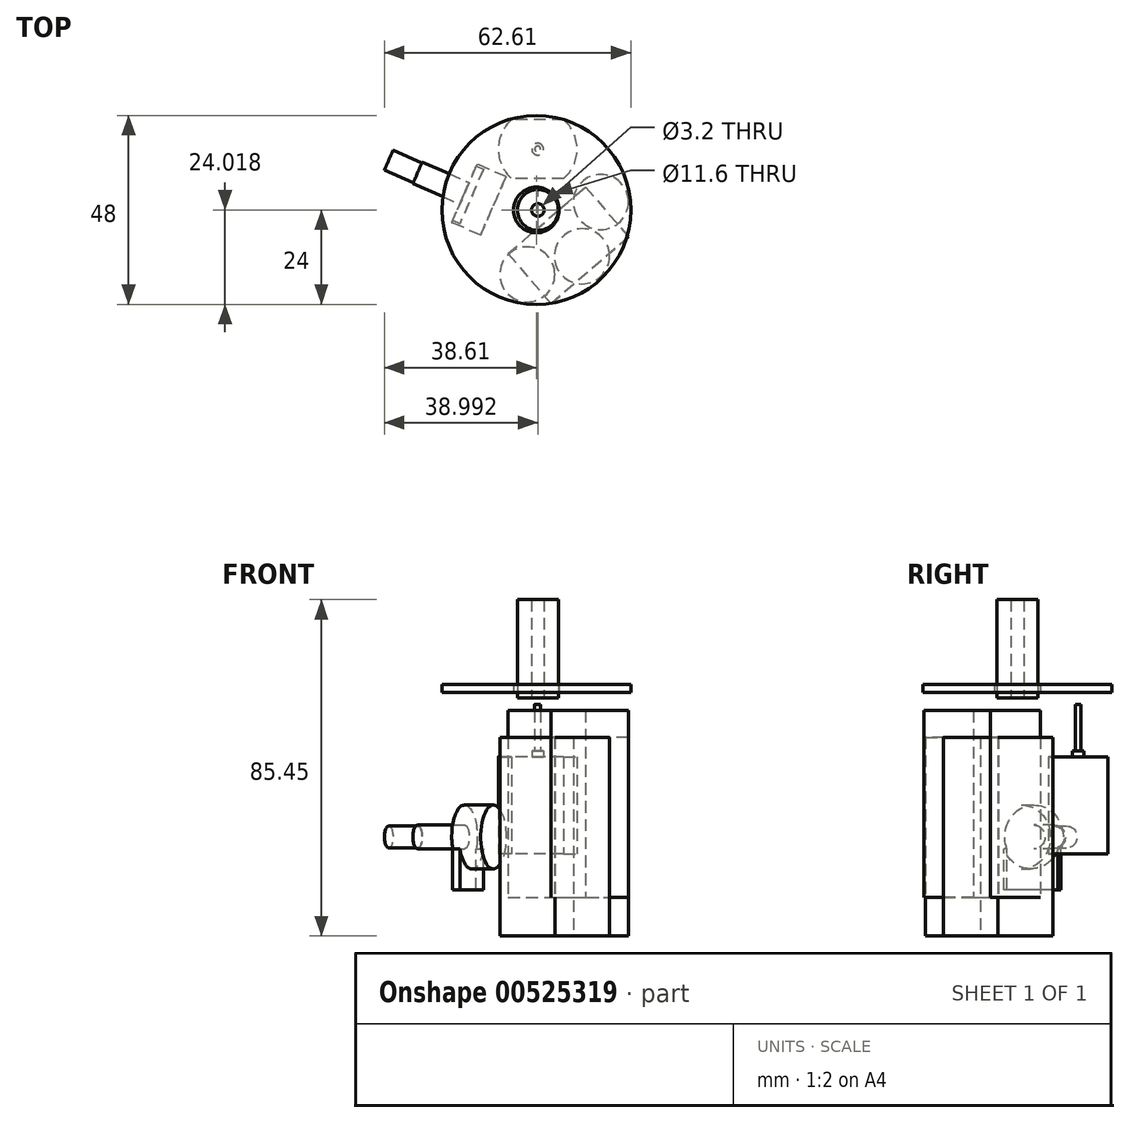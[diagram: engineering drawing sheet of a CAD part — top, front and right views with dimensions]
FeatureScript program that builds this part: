
annotation { "Feature Type Name" : "Feature", "Feature Type Description" : "" }
export const myFeature = defineFeature(function(context is Context, id is Id, definition is map)
    precondition{}
    {
        {
            var Q0;
            Q0=qCreatedBy(makeId("Top.planeOp"),FACE);
            var sketch = newSketch(context, id + "F0", { "sketchPlane" : qUnion([Q0])});
            skCircle(sketch, "E0", {"center": v(0, 0) * mm, "radius": 24 * mm});
            skCircle(sketch, "E1", {"center": v(0, 0) * mm, "radius": 5.8 * mm});
            skCircle(sketch, "E2", {"center": v(39.36, 34.71) * mm, "radius": 5.2 * mm});
            skCircle(sketch, "E3", {"center": v(39.36, 34.71) * mm, "radius": 1.6 * mm});
            skCircle(sketch, "E4", {"center": v(56.14, -22.76) * mm, "radius": 7 * mm});
            skCircle(sketch, "E5", {"center": v(-57.01, -53.17) * mm, "radius": 10 * mm});
            skLineSegment(sketch, "E6.bottom", {"start": v(-49.51, -39.98) * mm, "end": v(-64.51, -39.98) * mm, "construction": true});
            skLineSegment(sketch, "E6.top", {"start": v(-49.51, -66.36) * mm, "end": v(-64.51, -66.36) * mm, "construction": true});
            skLineSegment(sketch, "E6.left", {"start": v(-49.51, -39.98) * mm, "end": v(-49.51, -66.36) * mm});
            skLineSegment(sketch, "E6.right", {"start": v(-64.51, -39.98) * mm, "end": v(-64.51, -66.36) * mm});
            skLineSegment(sketch, "E7.bottom", {"start": v(21.26, -45.6) * mm, "end": v(47.26, -45.6) * mm});
            skLineSegment(sketch, "E7.top", {"start": v(21.26, -62.3) * mm, "end": v(47.26, -62.3) * mm});
            skLineSegment(sketch, "E7.left", {"start": v(21.26, -45.6) * mm, "end": v(21.26, -62.3) * mm});
            skLineSegment(sketch, "E7.right", {"start": v(47.26, -45.6) * mm, "end": v(47.26, -62.3) * mm});
            skCircle(sketch, "E8", {"center": v(-32.39, -87.84) * mm, "radius": 8.1 * mm});
            skLineSegment(sketch, "E9", {"start": v(-24.29, -87.84) * mm, "end": v(-45.79, -87.84) * mm, "construction": true});
            skLineSegment(sketch, "E10.bottom", {"start": v(-45.79, -80.34) * mm, "end": v(-18.99, -80.34) * mm, "construction": true});
            skLineSegment(sketch, "E10.top", {"start": v(-45.79, -95.34) * mm, "end": v(-18.99, -95.34) * mm, "construction": true});
            skLineSegment(sketch, "E10.left", {"start": v(-45.79, -80.34) * mm, "end": v(-45.79, -95.34) * mm});
            skLineSegment(sketch, "E10.right", {"start": v(-18.99, -80.34) * mm, "end": v(-18.99, -95.34) * mm, "construction": true});
            skLineSegment(sketch, "E11", {"start": v(-45.79, -95.34) * mm, "end": v(-35.45, -95.34) * mm});
            skLineSegment(sketch, "E12", {"start": v(-45.79, -80.34) * mm, "end": v(-35.45, -80.34) * mm});
            skSolve(sketch);
        }
        {
            var Q0;
            Q0=makeQuery(id+"F0.imprint","IMPRINT",FACE,{"disambiguationData":[TD([[makeQuery(id+"F0.imprint","IMPRINT",EDGE,{"derivedFrom":sQuery(id+"F0.wireOp",EDGE,"E0")}),1.0]])]});
            extrude(context, id + "F1", {"entities" : qUnion([Q0]), "depth" : 2 * mm, "offsetDistance" : 25 * mm});
        }
        {
            var Q0;
            Q0=makeQuery(id+"F0.imprint","IMPRINT",FACE,{"disambiguationData":[TD([[makeQuery(id+"F0.imprint","IMPRINT",EDGE,{"derivedFrom":sQuery(id+"F0.wireOp",EDGE,"E2")}),1.0]])]});
            extrude(context, id + "F2", {"entities" : qUnion([Q0]), "depth" : 25 * mm, "offsetDistance" : 25 * mm});
        }
        {
            var Q0;
            Q0=makeQuery(id+"F0.imprint","IMPRINT",FACE,{"disambiguationData":[TD([[makeQuery(id+"F0.imprint","IMPRINT",EDGE,{"derivedFrom":sQuery(id+"F0.wireOp",EDGE,"E4")}),1.0]])]});
            extrude(context, id + "F3", {"entities" : qUnion([Q0]), "depth" : 50.5 * mm, "offsetDistance" : 25 * mm});
        }
        {
            var Q0;
            Q0=makeQuery(id+"F0.imprint","IMPRINT",FACE,{"disambiguationData":[TD([[makeQuery(id+"F0.imprint","IMPRINT",EDGE,{"derivedFrom":sQuery(id+"F0.wireOp",EDGE,"E7.bottom")}),-1.0]])]});
            extrude(context, id + "F4", {"entities" : qUnion([Q0]), "depth" : 47.5 * mm, "offsetDistance" : 25 * mm});
        }
        {
            var Q0;
            {var subQ0=sQuery(id+"F0.wireOp",EDGE,"E6.right");var subQ1=sQuery(id+"F0.wireOp",EDGE,"E5");var subQ2=makeQuery(id+"F0.imprint","INTERSECT",VERTEX,{"disambiguationData":[OD(0.0)],"derivedFrom":[subQ1,subQ0]});Q0=makeQuery(id+"F0.imprint","IMPRINT",FACE,{"disambiguationData":[TD([[makeQuery(id+"F0.imprint","IMPRINT",EDGE,{"disambiguationData":[TD([[subQ2,1.0]])],"derivedFrom":subQ1}),1.0]])]});}
            extrude(context, id + "F5", {"entities" : qUnion([Q0]), "depth" : 24.7 * mm, "offsetDistance" : 25 * mm});
        }
        {
            var Q0;
            {var subQ0=sQuery(id+"F0.wireOp",EDGE,"E8");var subQ1=makeQuery(id+"F0.imprint","INTERSECT",VERTEX,{"derivedFrom":[subQ0,sQuery(id+"F0.wireOp",EDGE,"E11")]});Q0=makeQuery(id+"F0.imprint","IMPRINT",FACE,{"disambiguationData":[TD([[makeQuery(id+"F0.imprint","IMPRINT",EDGE,{"disambiguationData":[TD([[subQ1,1.0]])],"derivedFrom":subQ0}),1.0]])]});}
            extrude(context, id + "F6", {"entities" : qUnion([Q0]), "oppositeDirection" : true, "depth" : 6 * mm, "offsetDistance" : 25 * mm});
        }
        {
            var Q0;
            {var subQ0=sQuery(id+"F0.wireOp",EDGE,"E8");var subQ1=makeQuery(id+"F0.imprint","INTERSECT",VERTEX,{"derivedFrom":[subQ0,sQuery(id+"F0.wireOp",EDGE,"E11")]});Q0=makeQuery(id+"F0.imprint","IMPRINT",FACE,{"disambiguationData":[TD([[makeQuery(id+"F0.imprint","IMPRINT",EDGE,{"disambiguationData":[TD([[subQ1,1.0]])],"derivedFrom":subQ0}),1.0]])]});}
            var Q1;
            Q1=makeQuery(id+"F0.imprint","IMPRINT",FACE,{"disambiguationData":[TD([[makeQuery(id+"F0.imprint","IMPRINT",EDGE,{"derivedFrom":sQuery(id+"F0.wireOp",EDGE,"E10.left")}),1.0]])]});
            extrude(context, id + "F7", {"entities" : qUnion([Q0, Q1]), "operationType" : NewBodyOperationType.ADD, "depth" : 2 * mm, "offsetDistance" : 25 * mm});
        }
        {
            var Q0;
            Q0=makeQuery(id+"F5.opExtrude","CAP_FACE",FACE,{"disambiguationData":[OSD([sQuery(id+"F0.wireOp",EDGE,"E5"),sQuery(id+"F0.wireOp",EDGE,"E6.left"),sQuery(id+"F0.wireOp",EDGE,"E6.right")])],"isStart":false});
            var sketch = newSketch(context, id + "F8", { "sketchPlane" : qUnion([Q0])});
            skCircle(sketch, "E13", {"center": v(-57.01, -53.17) * mm, "radius": 0.75 * mm});
            skCircle(sketch, "E14", {"center": v(-57.01, -53.17) * mm, "radius": 1.5 * mm});
            skSolve(sketch);
        }
        {
            var Q0;
            Q0=makeQuery(id+"F8.imprint","IMPRINT",FACE,{"disambiguationData":[TD([[makeQuery(id+"F8.imprint","IMPRINT",EDGE,{"derivedFrom":sQuery(id+"F8.wireOp",EDGE,"E13")}),1.0]])]});
            extrude(context, id + "F9", {"entities" : qUnion([Q0]), "operationType" : NewBodyOperationType.ADD, "depth" : 13.3 * mm, "offsetDistance" : 25 * mm});
        }
        {
            var Q0;
            Q0=makeQuery(id+"F8.imprint","IMPRINT",FACE,{"disambiguationData":[TD([[makeQuery(id+"F8.imprint","IMPRINT",EDGE,{"derivedFrom":sQuery(id+"F8.wireOp",EDGE,"E13")}),-1.0]])]});
            extrude(context, id + "F10", {"entities" : qUnion([Q0]), "operationType" : NewBodyOperationType.ADD, "depth" : 1.5 * mm, "offsetDistance" : 25 * mm});
        }
        {
            var Q0;
            Q0=makeQuery(id+"F7.opExtrude","CAP_FACE",FACE,{"disambiguationData":[OSD([sQuery(id+"F0.wireOp",EDGE,"E8"),sQuery(id+"F0.wireOp",EDGE,"E10.left"),sQuery(id+"F0.wireOp",EDGE,"E11"),sQuery(id+"F0.wireOp",EDGE,"E12")])],"isStart":false});
            var sketch = newSketch(context, id + "F11", { "sketchPlane" : qUnion([Q0])});
            skCircle(sketch, "E15", {"center": v(-32.39, -87.84) * mm, "radius": 3 * mm});
            skSolve(sketch);
        }
        {
            var Q0;
            Q0 = qSketchRegion(id + "F11", true);
            extrude(context, id + "F12", {"entities" : qUnion([Q0]), "operationType" : NewBodyOperationType.ADD, "depth" : 21 * mm, "offsetDistance" : 25 * mm});
        }
        {
            var Q0;
            Q0=makeQuery(id+"F12.opExtrude","CAP_FACE",FACE,{"disambiguationData":[OSD([sQuery(id+"F11.wireOp",EDGE,"E15")])],"isStart":false});
            var sketch = newSketch(context, id + "F13", { "sketchPlane" : qUnion([Q0])});
            skCircle(sketch, "E16", {"center": v(-32.39, -87.84) * mm, "radius": 2.75 * mm});
            skSolve(sketch);
        }
        {
            var Q0;
            Q0=makeQuery(id+"F13.imprint","IMPRINT",FACE,{"disambiguationData":[TD([[makeQuery(id+"F13.imprint","IMPRINT",EDGE,{"derivedFrom":sQuery(id+"F13.wireOp",EDGE,"E16")}),-1.0]])]});
            extrude(context, id + "F14", {"entities" : qUnion([Q0]), "operationType" : NewBodyOperationType.REMOVE, "oppositeDirection" : true, "depth" : 8 * mm, "offsetDistance" : 25 * mm});
        }
        {
            var Q0;
            Q0=makeQuery(id+"F1.opExtrude","SWEPT_BODY",BODY,{"disambiguationData":[OSD([sQuery(id+"F0.wireOp",EDGE,"E0"),sQuery(id+"F0.wireOp",EDGE,"E1")])]});
            transform(context, id + "F15", {"entities" : qUnion([Q0]), "transformType" : TransformType.TRANSLATION_3D, "dx" : 0 * mm, "dy" : 0 * mm, "dz" : 52.12 * mm, "makeCopy" : false});
        }
        {
            var Q0;
            Q0=makeQuery(id+"F4.opExtrude","SWEPT_BODY",BODY,{"disambiguationData":[OSD([sQuery(id+"F0.wireOp",EDGE,"E7.bottom"),sQuery(id+"F0.wireOp",EDGE,"E7.top"),sQuery(id+"F0.wireOp",EDGE,"E7.left"),sQuery(id+"F0.wireOp",EDGE,"E7.right")])]});
            transform(context, id + "F16", {"entities" : qUnion([Q0]), "transformType" : TransformType.TRANSLATION_3D, "dx" : -34.19 * mm, "dy" : 42.18 * mm, "dz" : 0 * mm, "makeCopy" : false});
        }
        {
            var Q0;
            Q0=makeQuery(id+"F5.opExtrude","SWEPT_BODY",BODY,{"disambiguationData":[OSD([sQuery(id+"F0.wireOp",EDGE,"E5"),sQuery(id+"F0.wireOp",EDGE,"E6.left"),sQuery(id+"F0.wireOp",EDGE,"E6.right")])]});
            var Q1;
            {var subQ0=sQuery(id+"F0.wireOp",EDGE,"E5");Q1=makeQuery(id+"F5.opExtrude","SWEPT_FACE",FACE,{"disambiguationData":[OSD([subQ0]),TDD([makeQuery(id+"F0.imprint","IMPRINT",EDGE,{"disambiguationData":[TD([[makeQuery(id+"F0.imprint","INTERSECT",VERTEX,{"disambiguationData":[OD(1.0)],"derivedFrom":[subQ0,sQuery(id+"F0.wireOp",EDGE,"E6.right")]}),-1.0]])],"derivedFrom":subQ0})])]});}
            transform(context, id + "F17", {"entities" : qUnion([Q0]), "transformType" : TransformType.ROTATION, "transformAxis" : qUnion([Q1]), "angle" : 90 * degree, "makeCopy" : false});
        }
        {
            var Q0;
            Q0=makeQuery(id+"F5.opExtrude","SWEPT_BODY",BODY,{"disambiguationData":[OSD([sQuery(id+"F0.wireOp",EDGE,"E5"),sQuery(id+"F0.wireOp",EDGE,"E6.left"),sQuery(id+"F0.wireOp",EDGE,"E6.right")])]});
            transform(context, id + "F18", {"entities" : qUnion([Q0]), "transformType" : TransformType.TRANSLATION_3D, "dx" : 57.36 * mm, "dy" : 68.54 * mm, "dz" : 0 * mm, "makeCopy" : false});
        }
        {
            var Q0;
            Q0=makeQuery(id+"F5.opExtrude","SWEPT_BODY",BODY,{"disambiguationData":[OSD([sQuery(id+"F0.wireOp",EDGE,"E5"),sQuery(id+"F0.wireOp",EDGE,"E6.left"),sQuery(id+"F0.wireOp",EDGE,"E6.right")])]});
            transform(context, id + "F19", {"entities" : qUnion([Q0]), "transformType" : TransformType.TRANSLATION_3D, "dx" : 0 * mm, "dy" : 0.08 * mm, "dz" : 11.1 * mm, "makeCopy" : false});
        }
        {
            var Q0;
            Q0=makeQuery(id+"F2.opExtrude","SWEPT_BODY",BODY,{"disambiguationData":[OSD([sQuery(id+"F0.wireOp",EDGE,"E2"),sQuery(id+"F0.wireOp",EDGE,"E3")])]});
            transform(context, id + "F20", {"entities" : qUnion([Q0]), "transformType" : TransformType.TRANSLATION_3D, "dx" : 0 * mm, "dy" : -31.8 * mm, "dz" : 50.69 * mm, "makeCopy" : false});
        }
        {
            var Q0;
            Q0=makeQuery(id+"F2.opExtrude","SWEPT_BODY",BODY,{"disambiguationData":[OSD([sQuery(id+"F0.wireOp",EDGE,"E2"),sQuery(id+"F0.wireOp",EDGE,"E3")])]});
            transform(context, id + "F21", {"entities" : qUnion([Q0]), "transformType" : TransformType.TRANSLATION_3D, "dx" : -38.98 * mm, "dy" : -2.88 * mm, "dz" : 0 * mm, "makeCopy" : false});
        }
        {
            var Q0;
            Q0=makeQuery(id+"F6.opExtrude","SWEPT_BODY",BODY,{"disambiguationData":[OSD([sQuery(id+"F0.wireOp",EDGE,"E8")])]});
            var Q1;
            Q1=makeQuery(id+"F7.opExtrude","CAP_EDGE",EDGE,{"disambiguationData":[OSD([sQuery(id+"F0.wireOp",EDGE,"E10.left")])],"isStart":false});
            transform(context, id + "F22", {"entities" : qUnion([Q0]), "transformType" : TransformType.ROTATION, "transformAxis" : qUnion([Q1]), "angle" : 90 * degree, "makeCopy" : false});
        }
        {
            var Q0;
            Q0=makeQuery(id+"F6.opExtrude","SWEPT_BODY",BODY,{"disambiguationData":[OSD([sQuery(id+"F0.wireOp",EDGE,"E8")])]});
            var Q1;
            Q1=makeQuery(id+"F7.opExtrude","CAP_EDGE",EDGE,{"disambiguationData":[OSD([sQuery(id+"F0.wireOp",EDGE,"E11")])],"isStart":false});
            transform(context, id + "F23", {"entities" : qUnion([Q0]), "transformType" : TransformType.ROTATION, "transformAxis" : qUnion([Q1]), "angle" : 23.56 * degree, "oppositeDirection" : true, "makeCopy" : false});
        }
        {
            var Q0;
            Q0=makeQuery(id+"F6.opExtrude","SWEPT_BODY",BODY,{"disambiguationData":[OSD([sQuery(id+"F0.wireOp",EDGE,"E8")])]});
            transform(context, id + "F24", {"entities" : qUnion([Q0]), "transformType" : TransformType.TRANSLATION_3D, "dx" : 24.53 * mm, "dy" : 92.72 * mm, "dz" : 0 * mm, "makeCopy" : false});
        }
        {
            var Q0;
            Q0=makeQuery(id+"F4.opExtrude","SWEPT_BODY",BODY,{"disambiguationData":[OSD([sQuery(id+"F0.wireOp",EDGE,"E7.bottom"),sQuery(id+"F0.wireOp",EDGE,"E7.top"),sQuery(id+"F0.wireOp",EDGE,"E7.left"),sQuery(id+"F0.wireOp",EDGE,"E7.right")])]});
            var Q1;
            Q1=makeQuery(id+"F4.opExtrude","SWEPT_EDGE",EDGE,{"disambiguationData":[OSD([sQuery(id+"F0.wireOp",EDGE,"E7.bottom"),sQuery(id+"F0.wireOp",EDGE,"E7.right")])]});
            transform(context, id + "F25", {"entities" : qUnion([Q0]), "transformType" : TransformType.ROTATION, "transformAxis" : qUnion([Q1]), "angle" : 40.74 * degree, "oppositeDirection" : true, "makeCopy" : false});
        }
        {
            var Q0;
            Q0=makeQuery(id+"F4.opExtrude","SWEPT_BODY",BODY,{"disambiguationData":[OSD([sQuery(id+"F0.wireOp",EDGE,"E7.bottom"),sQuery(id+"F0.wireOp",EDGE,"E7.top"),sQuery(id+"F0.wireOp",EDGE,"E7.left"),sQuery(id+"F0.wireOp",EDGE,"E7.right")])]});
            transform(context, id + "F26", {"entities" : qUnion([Q0]), "transformType" : TransformType.TRANSLATION_3D, "dx" : -0.56 * mm, "dy" : 9.27 * mm, "dz" : 0 * mm, "makeCopy" : false});
        }
        {
            var Q0;
            Q0=makeQuery(id+"F3.opExtrude","SWEPT_BODY",BODY,{"disambiguationData":[OSD([sQuery(id+"F0.wireOp",EDGE,"E4")])]});
            transform(context, id + "F27", {"entities" : qUnion([Q0]), "transformType" : TransformType.TRANSLATION_3D, "dx" : 0 * mm, "dy" : 0 * mm, "dz" : -9.76 * mm, "makeCopy" : false});
        }
        {
            var Q0;
            Q0=makeQuery(id+"F3.opExtrude","SWEPT_BODY",BODY,{"disambiguationData":[OSD([sQuery(id+"F0.wireOp",EDGE,"E4")])]});
            transform(context, id + "F28", {"entities" : qUnion([Q0]), "transformType" : TransformType.TRANSLATION_3D, "dx" : -39.75 * mm, "dy" : 24.8 * mm, "dz" : 0 * mm, "makeCopy" : false});
        }
        {
            var Q0;
            Q0=makeQuery(id+"F3.opExtrude","SWEPT_BODY",BODY,{"disambiguationData":[OSD([sQuery(id+"F0.wireOp",EDGE,"E4")])]});
            var Q1;
            Q1=sQuery(id+"F0.wireOp",EDGE,"E0");
            circularPattern(context, id + "F29", {"entities" : qUnion([Q0]), "axis" : qUnion([Q1]), "angle" : 105 * degree, "instanceCount" : 3, "oppositeDirection" : true, "equalSpace" : true});
        }
    });
